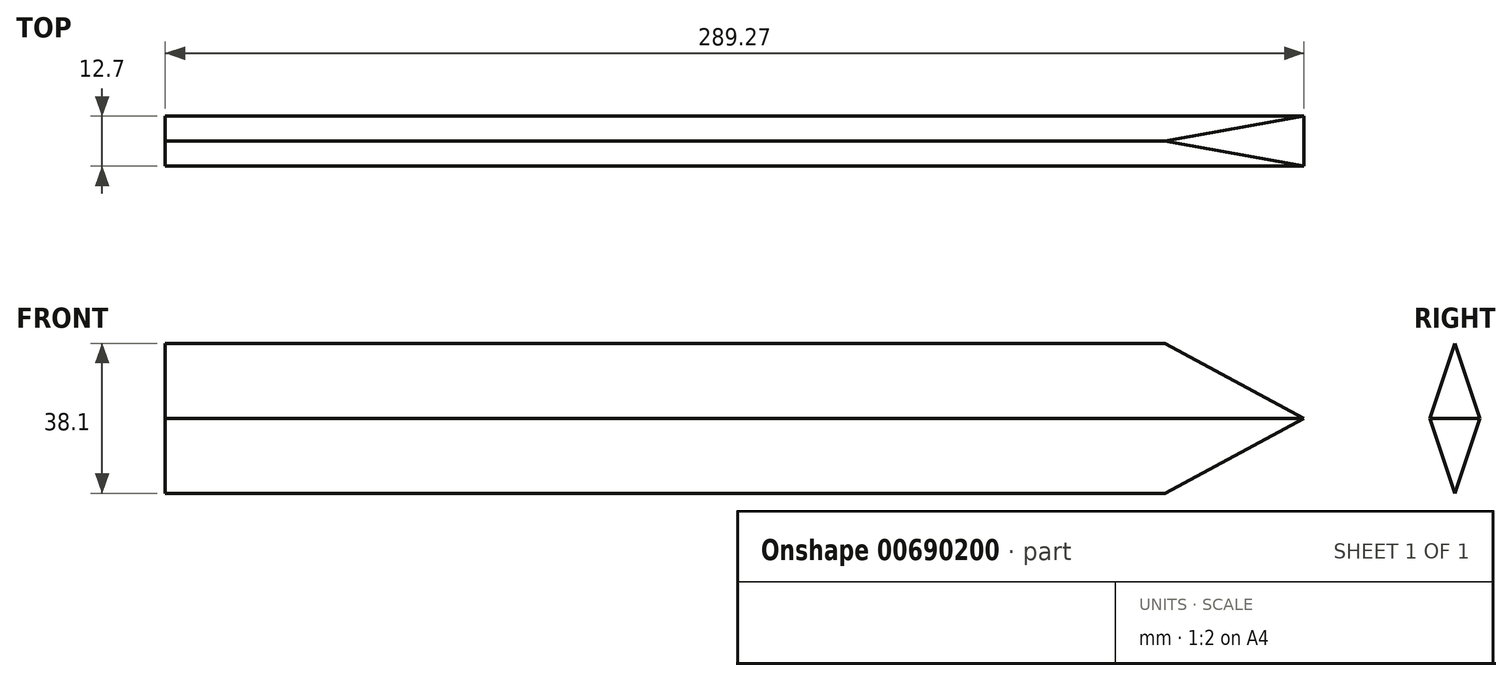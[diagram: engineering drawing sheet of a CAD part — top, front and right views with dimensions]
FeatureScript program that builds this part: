
annotation { "Feature Type Name" : "Feature", "Feature Type Description" : "" }
export const myFeature = defineFeature(function(context is Context, id is Id, definition is map)
    precondition{}
    {
        {
            var Q0;
            Q0=qCreatedBy(makeId("Front.planeOp"),FACE);
            var sketch = newSketch(context, id + "F0", { "sketchPlane" : qUnion([Q0])});
            skLineSegment(sketch, "E0.bottom", {"start": v(-127, 19.05) * mm, "end": v(127, 19.05) * mm});
            skLineSegment(sketch, "E0.top", {"start": v(-127, -19.05) * mm, "end": v(127, -19.05) * mm});
            skLineSegment(sketch, "E0.left", {"start": v(-127, 19.05) * mm, "end": v(-127, -19.05) * mm});
            skLineSegment(sketch, "E0.right", {"start": v(127, 19.05) * mm, "end": v(127, -19.05) * mm});
            skPoint(sketch, "E0.middle", {"position": v(0, 0) * mm});
            skLineSegment(sketch, "E1", {"start": v(0, 0) * mm, "end": v(162.27, 0) * mm});
            skLineSegment(sketch, "E2", {"start": v(162.27, 0) * mm, "end": v(127, -19.05) * mm});
            skLineSegment(sketch, "E3", {"start": v(162.27, 0) * mm, "end": v(127, 19.05) * mm});
            skLineSegment(sketch, "E4", {"start": v(0, 0) * mm, "end": v(0, 19.05) * mm});
            skLineSegment(sketch, "E5", {"start": v(0, 19.05) * mm, "end": v(0, -19.05) * mm});
            skSolve(sketch);
        }
        {
            var Q0;
            Q0 = qSketchRegion(id + "F0", true);
            extrude(context, id + "F1", {"entities" : qUnion([Q0]), "depth" : 12.7 * mm, "offsetDistance" : 25.4 * mm, "symmetric" : true});
        }
        {
            var Q0;
            Q0=makeQuery(id+"F1.opExtrude","SWEPT_FACE",FACE,{"disambiguationData":[OSD([sQuery(id+"F0.wireOp",EDGE,"E0.left")])]});
            var sketch = newSketch(context, id + "F2", { "sketchPlane" : qUnion([Q0])});
            skLineSegment(sketch, "E6", {"start": v(6.35, 0) * mm, "end": v(0, 19.05) * mm});
            skLineSegment(sketch, "E7", {"start": v(0, 19.05) * mm, "end": v(-6.35, 0) * mm});
            skLineSegment(sketch, "E8", {"start": v(-6.35, 0) * mm, "end": v(-6.35, 19.05) * mm});
            skLineSegment(sketch, "E9", {"start": v(-6.35, 19.05) * mm, "end": v(6.35, 19.05) * mm});
            skLineSegment(sketch, "E10", {"start": v(6.35, 19.05) * mm, "end": v(6.35, 0) * mm});
            skSolve(sketch);
        }
        {
            var Q0;
            Q0 = qSketchRegion(id + "F2", true);
            extrude(context, id + "F3", {"entities" : qUnion([Q0]), "operationType" : NewBodyOperationType.REMOVE, "oppositeDirection" : true, "depth" : 298.45 * mm, "offsetDistance" : 25.4 * mm});
        }
        {
            var Q0;
            Q0=makeQuery(id+"F1.opExtrude","SWEPT_FACE",FACE,{"disambiguationData":[OSD([sQuery(id+"F0.wireOp",EDGE,"E0.left")])]});
            var sketch = newSketch(context, id + "F4", { "sketchPlane" : qUnion([Q0])});
            skLineSegment(sketch, "E11.bottom", {"start": v(6.35, 0) * mm, "end": v(-6.35, 0) * mm});
            skLineSegment(sketch, "E11.top", {"start": v(6.35, -19.05) * mm, "end": v(-6.35, -19.05) * mm});
            skLineSegment(sketch, "E11.left", {"start": v(6.35, 0) * mm, "end": v(6.35, -19.05) * mm});
            skLineSegment(sketch, "E11.right", {"start": v(-6.35, 0) * mm, "end": v(-6.35, -19.05) * mm});
            skSolve(sketch);
        }
        {
            var Q0;
            Q0 = qSketchRegion(id + "F4", true);
            extrude(context, id + "F5", {"entities" : qUnion([Q0]), "operationType" : NewBodyOperationType.REMOVE, "oppositeDirection" : true, "depth" : 324.1 * mm, "offsetDistance" : 25.4 * mm});
        }
        {
            var Q0;
            Q0=makeQuery(id+"F1.opExtrude","SWEPT_BODY",BODY,{"disambiguationData":[OSD([sQuery(id+"F0.wireOp",EDGE,"E0.bottom"),sQuery(id+"F0.wireOp",EDGE,"E0.top"),sQuery(id+"F0.wireOp",EDGE,"E0.left"),sQuery(id+"F0.wireOp",EDGE,"E2"),sQuery(id+"F0.wireOp",EDGE,"E3")])]});
            var Q1;
            Q1=qCreatedBy(makeId("Top.planeOp"),FACE);
            mirror(context, id + "F6", {"operationType" : NewBodyOperationType.ADD, "entities" : qUnion([Q0]), "mirrorPlane" : qUnion([Q1])});
        }
    });
